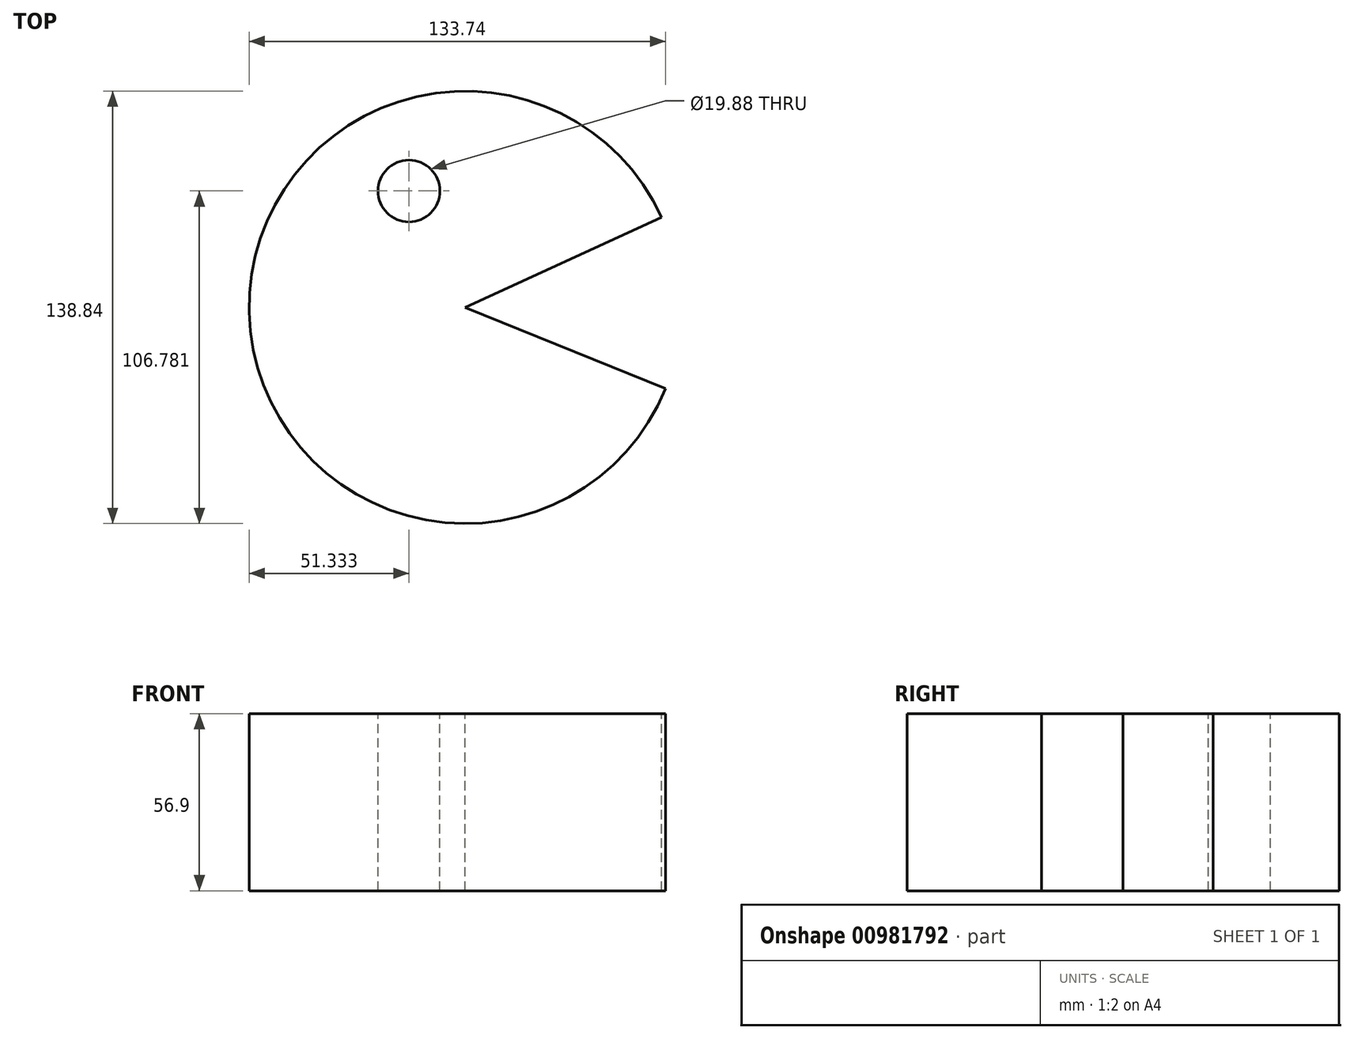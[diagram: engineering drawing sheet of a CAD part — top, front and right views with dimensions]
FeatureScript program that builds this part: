
annotation { "Feature Type Name" : "Feature", "Feature Type Description" : "" }
export const myFeature = defineFeature(function(context is Context, id is Id, definition is map)
    precondition{}
    {
        {
            var Q0;
            Q0=qCreatedBy(makeId("Top.planeOp"),FACE);
            var sketch = newSketch(context, id + "F0", { "sketchPlane" : qUnion([Q0])});
            skCircle(sketch, "E0", {"center": v(0, 0) * mm, "radius": 69.42 * mm});
            skSolve(sketch);
        }
        {
            var Q0;
            Q0 = qSketchRegion(id + "F0", true);
            extrude(context, id + "F1", {"entities" : qUnion([Q0]), "depth" : 56.9 * mm, "offsetDistance" : 25.4 * mm});
        }
        {
            var Q0;
            Q0=makeQuery(id+"F1.opExtrude","CAP_FACE",FACE,{"disambiguationData":[OSD([sQuery(id+"F0.wireOp",EDGE,"E0")])],"isStart":false});
            var sketch = newSketch(context, id + "F2", { "sketchPlane" : qUnion([Q0])});
            skLineSegment(sketch, "E1", {"start": v(0, 0) * mm, "end": v(63.12, 28.9) * mm});
            skLineSegment(sketch, "E2", {"start": v(0, 0) * mm, "end": v(64.32, -26.13) * mm});
            skCircle(sketch, "E3", {"center": v(-18.09, 37.36) * mm, "radius": 9.94 * mm});
            skSolve(sketch);
        }
        {
            var Q0;
            {var subQ0=sQuery(id+"F2.wireOp",EDGE,"E1");Q0=makeQuery(id+"F2.imprint","IMPRINT",FACE,{"disambiguationData":[TD([[makeQuery(id+"F2.imprint","IMPRINT",EDGE,{"derivedFrom":subQ0}),-1.0]])]});}
            var Q1;
            Q1=makeQuery(id+"F2.imprint","IMPRINT",FACE,{"disambiguationData":[TD([[makeQuery(id+"F2.imprint","IMPRINT",EDGE,{"derivedFrom":sQuery(id+"F2.wireOp",EDGE,"E3")}),1.0]])]});
            extrude(context, id + "F3", {"entities" : qUnion([Q0, Q1]), "operationType" : NewBodyOperationType.REMOVE, "endBound" : BoundingType.THROUGH_ALL, "oppositeDirection" : true, "depth" : 25.4 * mm, "offsetDistance" : 25.4 * mm});
        }
    });
